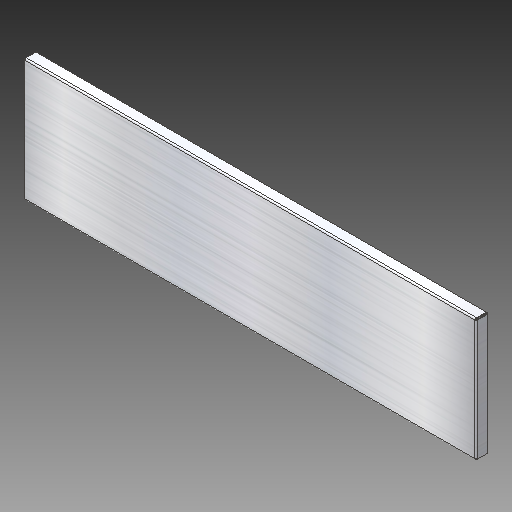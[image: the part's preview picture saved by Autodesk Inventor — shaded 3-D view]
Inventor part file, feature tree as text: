
AUTODESK INVENTOR PART (.ipt)
format: ipt  version: 2017 (Build 210142000, 142)  size: 428,544 bytes
history: native  units: mm
features: sheet_metal_op x8, sketch x7, other x5, plane x1
ambient origin geometry x8: Origin, YZ Plane, XZ Plane, XY Plane, X Axis, Y Axis, Z Axis, Center Point
bodies: Solid1 (feature_tree)
feature tree (21):
  sheet_metal_op  "Face1"
  sheet_metal_op  "Flange1"
  sheet_metal_op  "Hem1"
  sheet_metal_op  "Hem2"
  sheet_metal_op  "Hem3"
  sheet_metal_op  "Hem4"
  plane  "Work Plane1"
  other  "Decal1"
  sketch  "Sketch1"  dims[d0=253.299mm]
  other  "Plate1"
  sketch  "Sketch2"  dims[d1=933.598mm]
  other  "Plate2"
  sheet_metal_op  "Bend1"
  sheet_metal_op  "Corner1"
  sketch  "Sketch7"  dims[d6=1.5mm d7=25.0mm d8=90.0deg d9=1.5mm d10=6.0mm d11=1.5mm d12=1.5mm d13=1.5mm d14=0.75mm d15=3.0mm d16=1.5mm d17=10.0mm d18=0.75mm d19=0.375mm d20=1.5mm d21=0.75mm d22=3.0mm d23=1.5mm d24=10.0mm d25=0.75mm d26=0.375mm d27=1.5mm d28=0.75mm d29=3.0mm d30=1.5mm d31=245.0mm d32=10.0mm d33=0.75mm d34=0.375mm d35=1.5mm d36=0.75mm d37=3.0mm d38=1.5mm d39=245.0mm d40=10.0mm d41=0.75mm d42=0.375mm d43=200.0mm]
  other  "Image1"
  sketch  "Sketch3"  dims[d2=1.5mm]
  sketch  "Sketch4"  dims[d3=1.5mm]
  sketch  "Sketch5"  dims[d4=0.75mm]
  sketch  "Sketch6"  dims[d5=3.0mm]
  other  "Definition1"
